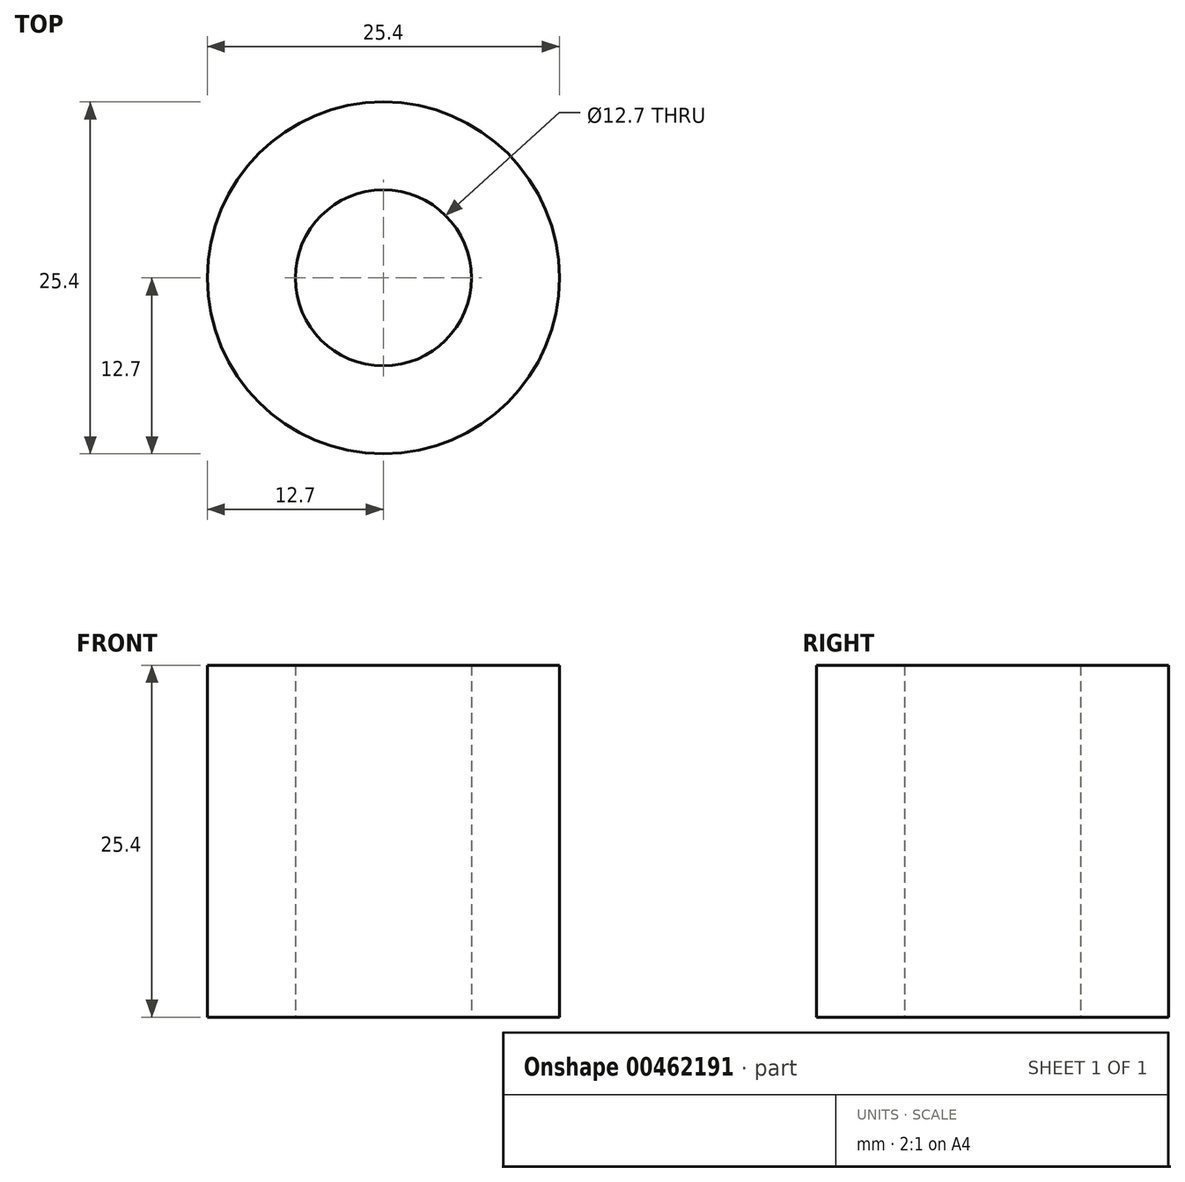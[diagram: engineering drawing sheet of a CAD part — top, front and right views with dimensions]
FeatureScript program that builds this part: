
annotation { "Feature Type Name" : "Feature", "Feature Type Description" : "" }
export const myFeature = defineFeature(function(context is Context, id is Id, definition is map)
    precondition{}
    {
        {
            var Q0;
            Q0=qCreatedBy(makeId("Top.planeOp"),FACE);
            var sketch = newSketch(context, id + "F0", { "sketchPlane" : qUnion([Q0])});
            skCircle(sketch, "E0", {"center": v(0, 0) * mm, "radius": 12.7 * mm});
            skCircle(sketch, "E1", {"center": v(0, 0) * mm, "radius": 6.35 * mm});
            skSolve(sketch);
        }
        {
            var Q0;
            Q0 = qSketchRegion(id + "F0", true);
            extrude(context, id + "F1", {"entities" : qUnion([Q0]), "depth" : 25.4 * mm});
        }
    });
